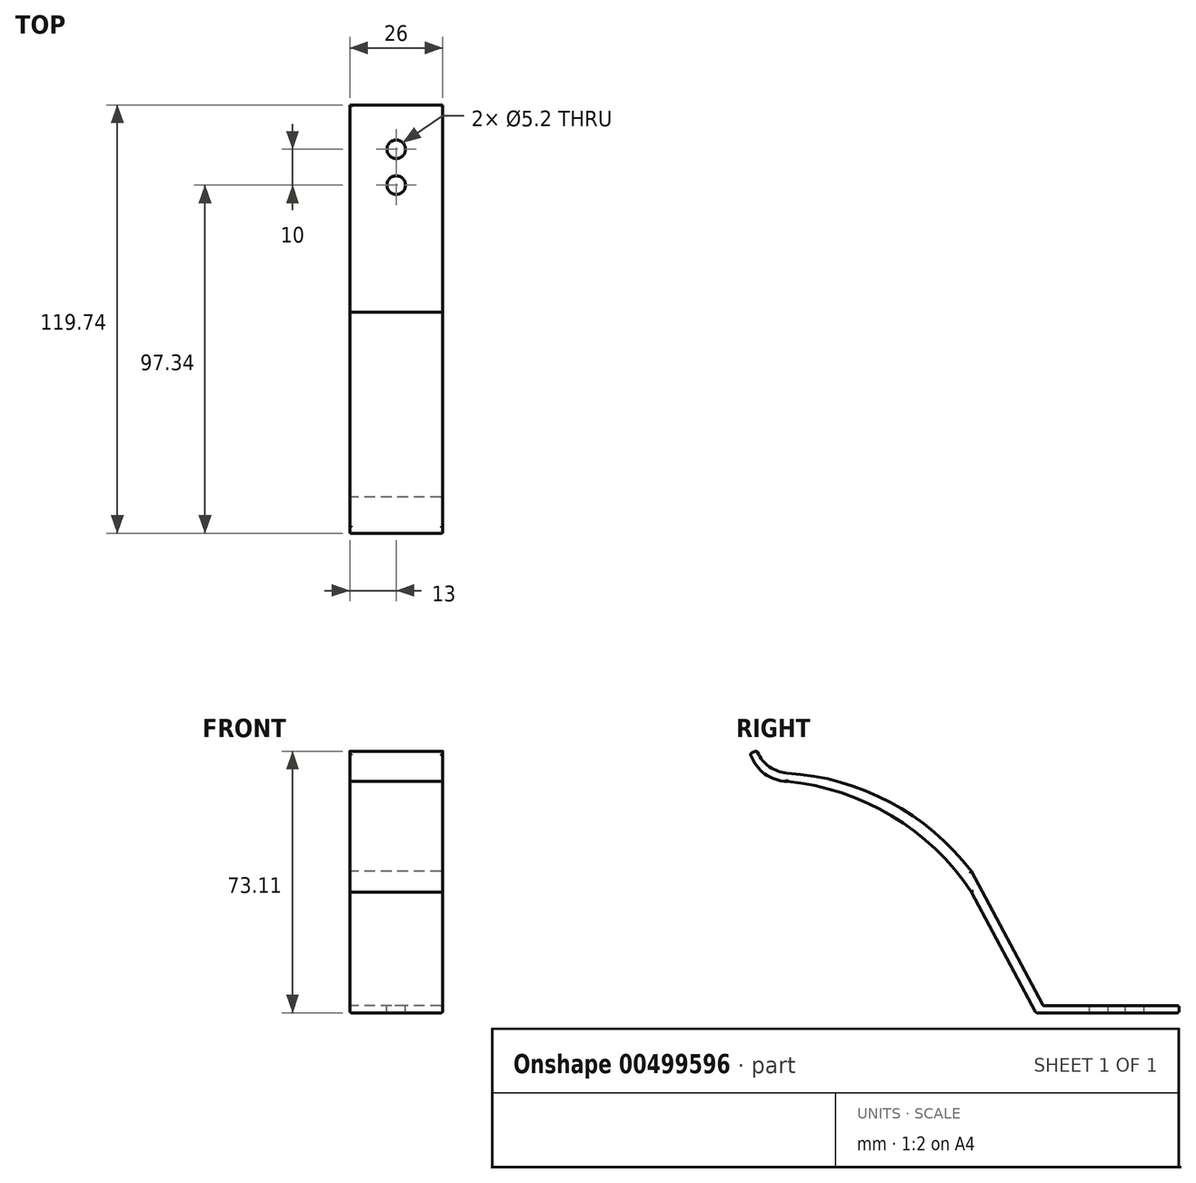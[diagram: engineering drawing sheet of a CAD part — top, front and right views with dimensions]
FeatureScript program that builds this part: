
annotation { "Feature Type Name" : "Feature", "Feature Type Description" : "" }
export const myFeature = defineFeature(function(context is Context, id is Id, definition is map)
    precondition{}
    {
        {
            var Q0;
            Q0=qCreatedBy(makeId("Right.planeOp"),FACE);
            var sketch = newSketch(context, id + "F0", { "sketchPlane" : qUnion([Q0])});
            skLineSegment(sketch, "E0", {"start": v(0, 0) * mm, "end": v(-5, 0) * mm});
            skArc(sketch, "E1", {"start": v(-25, 37.52) * mm, "mid": v(-47.8, 56.91) * mm, "end": v(-76.62, 65.01) * mm});
            skLineSegment(sketch, "E2", {"start": v(-25, 37.52) * mm, "end": v(-5, 0) * mm});
            skArc(sketch, "E3", {"start": v(-25, 31.78) * mm, "mid": v(-47.32, 53.07) * mm, "end": v(-76.62, 62.7) * mm});
            skLineSegment(sketch, "E4", {"start": v(-25, 31.78) * mm, "end": v(-6.99, -2) * mm});
            skPoint(sketch, "E5.end.orphan", {"position": v(3.31, -2) * mm});
            skLineSegment(sketch, "E6", {"start": v(-6.99, -2) * mm, "end": v(0, -2) * mm});
            skLineSegment(sketch, "E7", {"start": v(0, -2) * mm, "end": v(33, -2) * mm});
            skLineSegment(sketch, "E8", {"start": v(33, -2) * mm, "end": v(33, 0) * mm});
            skLineSegment(sketch, "E9", {"start": v(33, 0) * mm, "end": v(0, 0) * mm});
            skArc(sketch, "E10", {"start": v(-85, 71.26) * mm, "mid": v(-81.7, 66.95) * mm, "end": v(-76.62, 65.01) * mm});
            skPoint(sketch, "E11.end.orphan", {"position": v(-85, 63) * mm});
            skLineSegment(sketch, "E12", {"start": v(-85, 71.26) * mm, "end": v(-86.86, 70.52) * mm});
            skPoint(sketch, "E13.trimOffspring.end.orphan", {"position": v(-85, 65) * mm});
            skPoint(sketch, "E14.start.orphan", {"position": v(-85, 68.48) * mm});
            skArc(sketch, "E15", {"start": v(-86.86, 70.52) * mm, "mid": v(-83, 64.96) * mm, "end": v(-76.62, 62.7) * mm});
            skSolve(sketch);
        }
        {
            var Q0;
            Q0 = qSketchRegion(id + "F0", true);
            extrude(context, id + "F1", {"entities" : qUnion([Q0]), "depth" : 26 * mm});
        }
        {
            var Q0;
            Q0=makeQuery(id+"F1.opExtrude","SWEPT_FACE",FACE,{"disambiguationData":[OSD([sQuery(id+"F0.wireOp",EDGE,"E0"),sQuery(id+"F0.wireOp",EDGE,"E9")])]});
            var sketch = newSketch(context, id + "F2", { "sketchPlane" : qUnion([Q0])});
            skCircle(sketch, "E16", {"center": v(13, 10.6) * mm, "radius": 2.6 * mm});
            skCircle(sketch, "E17", {"center": v(13, 20.6) * mm, "radius": 2.6 * mm});
            skSolve(sketch);
        }
        {
            var Q0;
            Q0 = qSketchRegion(id + "F2", true);
            extrude(context, id + "F3", {"entities" : qUnion([Q0]), "operationType" : NewBodyOperationType.REMOVE, "oppositeDirection" : true, "depth" : 25 * mm});
        }
        {
            var Q0;
            Q0=makeQuery(id+"F1.opExtrude","CAP_EDGE",EDGE,{"disambiguationData":[OSD([sQuery(id+"F0.wireOp",EDGE,"E0"),sQuery(id+"F0.wireOp",EDGE,"E9")])],"isStart":true});
            var Q1;
            Q1=makeQuery(id+"F1.opExtrude","CAP_EDGE",EDGE,{"disambiguationData":[OSD([sQuery(id+"F0.wireOp",EDGE,"E6"),sQuery(id+"F0.wireOp",EDGE,"E7")])],"isStart":false});
            var Q2;
            Q2=makeQuery(id+"F1.opExtrude","CAP_EDGE",EDGE,{"disambiguationData":[OSD([sQuery(id+"F0.wireOp",EDGE,"E0"),sQuery(id+"F0.wireOp",EDGE,"E9")])],"isStart":false});
            var Q3;
            Q3=makeQuery(id+"F1.opExtrude","SWEPT_EDGE",EDGE,{"disambiguationData":[OSD([sQuery(id+"F0.wireOp",EDGE,"E8"),sQuery(id+"F0.wireOp",EDGE,"E9")])]});
            var Q4;
            Q4=makeQuery(id+"F1.opExtrude","SWEPT_EDGE",EDGE,{"disambiguationData":[OSD([sQuery(id+"F0.wireOp",EDGE,"E7"),sQuery(id+"F0.wireOp",EDGE,"E8")])]});
            var Q5;
            Q5=makeQuery(id+"F1.opExtrude","SWEPT_EDGE",EDGE,{"disambiguationData":[OSD([sQuery(id+"F0.wireOp",EDGE,"E0"),sQuery(id+"F0.wireOp",EDGE,"E2")])]});
            var Q6;
            Q6=makeQuery(id+"F1.opExtrude","SWEPT_EDGE",EDGE,{"disambiguationData":[OSD([sQuery(id+"F0.wireOp",EDGE,"E4"),sQuery(id+"F0.wireOp",EDGE,"E6")])]});
            var Q7;
            Q7=makeQuery(id+"F1.opExtrude","CAP_EDGE",EDGE,{"disambiguationData":[OSD([sQuery(id+"F0.wireOp",EDGE,"E6"),sQuery(id+"F0.wireOp",EDGE,"E7")])],"isStart":true});
            var Q8;
            Q8=makeQuery(id+"F1.opExtrude","CAP_EDGE",EDGE,{"disambiguationData":[OSD([sQuery(id+"F0.wireOp",EDGE,"E2")])],"isStart":false});
            var Q9;
            Q9=makeQuery(id+"F1.opExtrude","CAP_EDGE",EDGE,{"disambiguationData":[OSD([sQuery(id+"F0.wireOp",EDGE,"E4")])],"isStart":false});
            var Q10;
            Q10=makeQuery(id+"F1.opExtrude","CAP_EDGE",EDGE,{"disambiguationData":[OSD([sQuery(id+"F0.wireOp",EDGE,"E2")])],"isStart":true});
            var Q11;
            Q11=makeQuery(id+"F1.opExtrude","CAP_EDGE",EDGE,{"disambiguationData":[OSD([sQuery(id+"F0.wireOp",EDGE,"E4")])],"isStart":true});
            var Q12;
            Q12=makeQuery(id+"F1.opExtrude","CAP_EDGE",EDGE,{"disambiguationData":[OSD([sQuery(id+"F0.wireOp",EDGE,"E1")])],"isStart":false});
            var Q13;
            Q13=makeQuery(id+"F1.opExtrude","CAP_EDGE",EDGE,{"disambiguationData":[OSD([sQuery(id+"F0.wireOp",EDGE,"E3")])],"isStart":false});
            var Q14;
            Q14=makeQuery(id+"F1.opExtrude","CAP_EDGE",EDGE,{"disambiguationData":[OSD([sQuery(id+"F0.wireOp",EDGE,"E3")])],"isStart":true});
            var Q15;
            Q15=makeQuery(id+"F1.opExtrude","CAP_EDGE",EDGE,{"disambiguationData":[OSD([sQuery(id+"F0.wireOp",EDGE,"E1")])],"isStart":true});
            var Q16;
            Q16=makeQuery(id+"F1.opExtrude","CAP_EDGE",EDGE,{"disambiguationData":[OSD([sQuery(id+"F0.wireOp",EDGE,"E14")])],"isStart":true});
            var Q17;
            Q17=makeQuery(id+"F1.opExtrude","CAP_EDGE",EDGE,{"disambiguationData":[OSD([sQuery(id+"F0.wireOp",EDGE,"E10")])],"isStart":true});
            var Q18;
            Q18=makeQuery(id+"F1.opExtrude","SWEPT_EDGE",EDGE,{"disambiguationData":[OSD([sQuery(id+"F0.wireOp",EDGE,"E10"),sQuery(id+"F0.wireOp",EDGE,"45331051-406c-4803-859f-b2bcacc74f95")])]});
            var Q19;
            Q19=makeQuery(id+"F1.opExtrude","SWEPT_EDGE",EDGE,{"disambiguationData":[OSD([sQuery(id+"F0.wireOp",EDGE,"E14"),sQuery(id+"F0.wireOp",EDGE,"45331051-406c-4803-859f-b2bcacc74f95")])]});
            var Q20;
            Q20=makeQuery(id+"F1.opExtrude","CAP_EDGE",EDGE,{"disambiguationData":[OSD([sQuery(id+"F0.wireOp",EDGE,"E14")])],"isStart":false});
            var Q21;
            Q21=makeQuery(id+"F1.opExtrude","CAP_EDGE",EDGE,{"disambiguationData":[OSD([sQuery(id+"F0.wireOp",EDGE,"E10")])],"isStart":false});
            var Q22;
            Q22=makeQuery(id+"F1.opExtrude","CAP_EDGE",EDGE,{"disambiguationData":[OSD([sQuery(id+"F0.wireOp",EDGE,"45331051-406c-4803-859f-b2bcacc74f95")])],"isStart":false});
            var Q23;
            Q23=makeQuery(id+"F1.opExtrude","CAP_EDGE",EDGE,{"disambiguationData":[OSD([sQuery(id+"F0.wireOp",EDGE,"45331051-406c-4803-859f-b2bcacc74f95")])],"isStart":true});
            var Q24;
            Q24=makeQuery(id+"F1.opExtrude","CAP_EDGE",EDGE,{"disambiguationData":[OSD([sQuery(id+"F0.wireOp",EDGE,"E15")])],"isStart":true});
            var Q25;
            Q25=makeQuery(id+"F1.opExtrude","CAP_EDGE",EDGE,{"disambiguationData":[OSD([sQuery(id+"F0.wireOp",EDGE,"E15")])],"isStart":false});
            var Q26;
            Q26=makeQuery(id+"F1.opExtrude","SWEPT_EDGE",EDGE,{"disambiguationData":[OSD([sQuery(id+"F0.wireOp",EDGE,"E10"),sQuery(id+"F0.wireOp",EDGE,"E12")])]});
            var Q27;
            Q27=makeQuery(id+"F1.opExtrude","SWEPT_EDGE",EDGE,{"disambiguationData":[OSD([sQuery(id+"F0.wireOp",EDGE,"E12"),sQuery(id+"F0.wireOp",EDGE,"E15")])]});
            fillet(context, id + "F4", {"entities" : qUnion([Q0, Q1, Q2, Q3, Q4, Q5, Q6, Q7, Q8, Q9, Q10, Q11, Q12, Q13, Q14, Q15, Q16, Q17, Q18, Q19, Q20, Q21, Q22, Q23, Q24, Q25, Q26, Q27]), "radius" : 0.5 * mm, "tangentPropagation" : true, "allowEdgeOverflow" : false});
        }
    });
